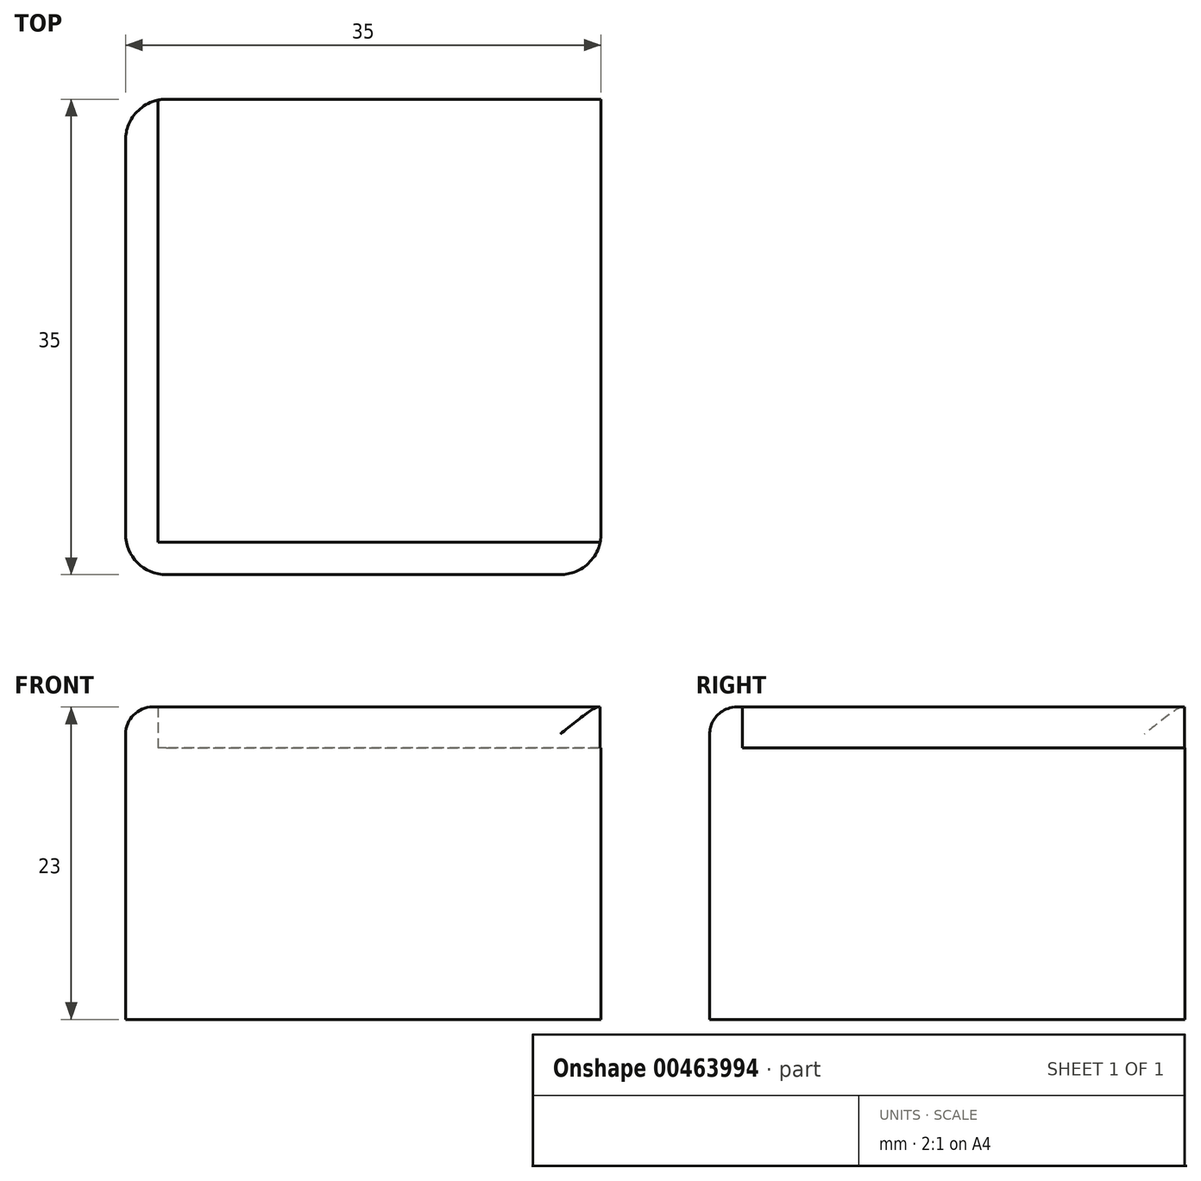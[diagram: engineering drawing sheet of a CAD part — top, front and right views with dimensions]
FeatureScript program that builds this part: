
annotation { "Feature Type Name" : "Feature", "Feature Type Description" : "" }
export const myFeature = defineFeature(function(context is Context, id is Id, definition is map)
    precondition{}
    {
        {
            var Q0;
            Q0=qCreatedBy(makeId("Top.planeOp"),FACE);
            var sketch = newSketch(context, id + "F0", { "sketchPlane" : qUnion([Q0])});
            skLineSegment(sketch, "E0.bottom", {"start": v(-17.5, 17.5) * mm, "end": v(17.5, 17.5) * mm});
            skLineSegment(sketch, "E0.top", {"start": v(-17.5, -17.5) * mm, "end": v(17.5, -17.5) * mm});
            skLineSegment(sketch, "E0.left", {"start": v(-17.5, 17.5) * mm, "end": v(-17.5, -17.5) * mm});
            skLineSegment(sketch, "E0.right", {"start": v(17.5, 17.5) * mm, "end": v(17.5, -17.5) * mm});
            skLineSegment(sketch, "E1", {"start": v(-15.1, 17.5) * mm, "end": v(-15.1, -15.1) * mm});
            skLineSegment(sketch, "E2", {"start": v(-15.1, -15.1) * mm, "end": v(17.5, -15.1) * mm});
            skSolve(sketch);
        }
        {
            var Q0;
            {var subQ3=sQuery(id+"F0.wireOp",EDGE,"E1");Q0=makeQuery(id+"F0.imprint","IMPRINT",FACE,{"disambiguationData":[TD([[makeQuery(id+"F0.imprint","IMPRINT",EDGE,{"derivedFrom":subQ3}),1.0]])]});}
            var Q1;
            {var subQ1=sQuery(id+"F0.wireOp",EDGE,"E0.top");Q1=makeQuery(id+"F0.imprint","IMPRINT",FACE,{"disambiguationData":[TD([[makeQuery(id+"F0.imprint","IMPRINT",EDGE,{"derivedFrom":subQ1}),1.0]])]});}
            extrude(context, id + "F1", {"entities" : qUnion([Q0, Q1]), "depth" : 10 * mm});
        }
        {
            var Q0;
            {var subQ1=sQuery(id+"F0.wireOp",EDGE,"E0.top");Q0=makeQuery(id+"F0.imprint","IMPRINT",FACE,{"disambiguationData":[TD([[makeQuery(id+"F0.imprint","IMPRINT",EDGE,{"derivedFrom":subQ1}),1.0]])]});}
            extrude(context, id + "F2", {"entities" : qUnion([Q0]), "operationType" : NewBodyOperationType.ADD, "depth" : 13 * mm});
        }
        {
            var Q0;
            Q0=makeQuery(id+"F2.opExtrude","CAP_EDGE",EDGE,{"disambiguationData":[OSD([sQuery(id+"F0.wireOp",EDGE,"E0.left")])],"isStart":false});
            var Q1;
            Q1=makeQuery(id+"F2.opExtrude","CAP_EDGE",EDGE,{"disambiguationData":[OSD([sQuery(id+"F0.wireOp",EDGE,"E0.top")])],"isStart":false});
            fillet(context, id + "F3", {"entities" : qUnion([Q0, Q1]), "radius" : 2 * mm, "tangentPropagation" : true, "allowEdgeOverflow" : false});
        }
        {
            var Q0;
            {var subQ0=sQuery(id+"F0.wireOp",EDGE,"E0.left");var subQ1=sQuery(id+"F0.wireOp",EDGE,"E0.top");Q0=makeQuery(id+"F2.boolean.opBoolean","MERGE",EDGE,{"derivedFrom":[makeQuery(id+"F1.opExtrude","SWEPT_EDGE",EDGE,{"disambiguationData":[OSD([subQ1,subQ0])]}),makeQuery(id+"F2.opExtrude","SWEPT_EDGE",EDGE,{"disambiguationData":[OSD([subQ1,subQ0])]})]});}
            var Q1;
            {var subQ0=sQuery(id+"F0.wireOp",EDGE,"E0.left");var subQ1=sQuery(id+"F0.wireOp",EDGE,"E0.bottom");Q1=makeQuery(id+"F2.boolean.opBoolean","MERGE",EDGE,{"derivedFrom":[makeQuery(id+"F1.opExtrude","SWEPT_EDGE",EDGE,{"disambiguationData":[OSD([subQ1,subQ0])]}),makeQuery(id+"F2.opExtrude","SWEPT_EDGE",EDGE,{"disambiguationData":[OSD([subQ1,subQ0])]})]});}
            var Q2;
            {var subQ0=sQuery(id+"F0.wireOp",EDGE,"E0.right");var subQ1=sQuery(id+"F0.wireOp",EDGE,"E0.top");Q2=makeQuery(id+"F2.boolean.opBoolean","MERGE",EDGE,{"derivedFrom":[makeQuery(id+"F1.opExtrude","SWEPT_EDGE",EDGE,{"disambiguationData":[OSD([subQ1,subQ0])]}),makeQuery(id+"F2.opExtrude","SWEPT_EDGE",EDGE,{"disambiguationData":[OSD([subQ1,subQ0])]})]});}
            fillet(context, id + "F4", {"entities" : qUnion([Q0, Q1, Q2]), "radius" : 3 * mm, "tangentPropagation" : true, "allowEdgeOverflow" : false});
        }
        {
            var Q0;
            {var subQ3=sQuery(id+"F0.wireOp",EDGE,"E1");Q0=makeQuery(id+"F0.imprint","IMPRINT",FACE,{"disambiguationData":[TD([[makeQuery(id+"F0.imprint","IMPRINT",EDGE,{"derivedFrom":subQ3}),1.0]])]});}
            var Q1;
            {var subQ1=sQuery(id+"F0.wireOp",EDGE,"E0.top");Q1=makeQuery(id+"F0.imprint","IMPRINT",FACE,{"disambiguationData":[TD([[makeQuery(id+"F0.imprint","IMPRINT",EDGE,{"derivedFrom":subQ1}),1.0]])]});}
            extrude(context, id + "F5", {"entities" : qUnion([Q0, Q1]), "operationType" : NewBodyOperationType.ADD, "oppositeDirection" : true, "depth" : 10 * mm});
        }
        {
            var Q0;
            Q0=makeQuery(id+"F5.opExtrude","SWEPT_EDGE",EDGE,{"disambiguationData":[OSD([sQuery(id+"F0.wireOp",EDGE,"E0.top"),sQuery(id+"F0.wireOp",EDGE,"E0.left")])]});
            var Q1;
            Q1=makeQuery(id+"F5.opExtrude","SWEPT_EDGE",EDGE,{"disambiguationData":[OSD([sQuery(id+"F0.wireOp",EDGE,"E0.top"),sQuery(id+"F0.wireOp",EDGE,"E0.right")])]});
            var Q2;
            Q2=makeQuery(id+"F5.opExtrude","SWEPT_EDGE",EDGE,{"disambiguationData":[OSD([sQuery(id+"F0.wireOp",EDGE,"E0.bottom"),sQuery(id+"F0.wireOp",EDGE,"E0.left")])]});
            fillet(context, id + "F6", {"entities" : qUnion([Q0, Q1, Q2]), "radius" : 3 * mm, "tangentPropagation" : true, "allowEdgeOverflow" : false});
        }
    });
